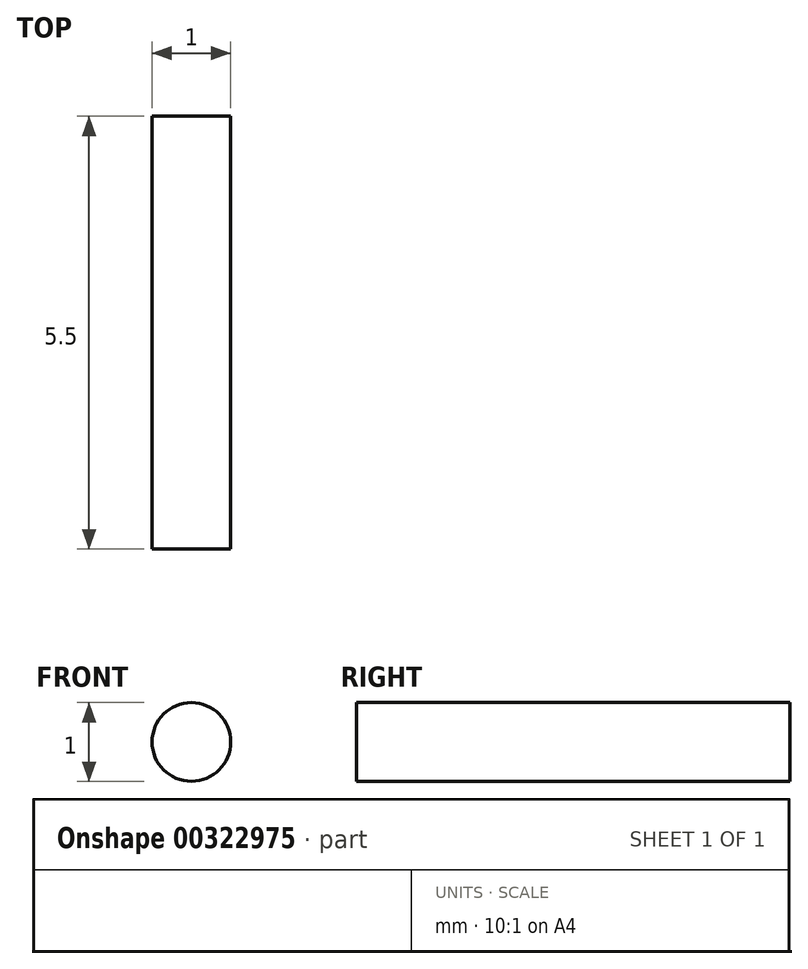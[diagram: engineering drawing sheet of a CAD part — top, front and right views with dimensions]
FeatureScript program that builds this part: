
annotation { "Feature Type Name" : "Feature", "Feature Type Description" : "" }
export const myFeature = defineFeature(function(context is Context, id is Id, definition is map)
    precondition{}
    {
        {
            var Q0;
            Q0=qCreatedBy(makeId("Front.planeOp"),FACE);
            var sketch = newSketch(context, id + "F0", { "sketchPlane" : qUnion([Q0])});
            skCircle(sketch, "E0", {"center": v(0, 0) * mm, "radius": 0.5 * mm});
            skSolve(sketch);
        }
        {
            var Q0;
            Q0=makeQuery(id+"F0.imprint","IMPRINT",FACE,{"disambiguationData":[TD([[makeQuery(id+"F0.imprint","IMPRINT",EDGE,{"derivedFrom":sQuery(id+"F0.wireOp",EDGE,"E0")}),1.0]])]});
            extrude(context, id + "F1", {"entities" : qUnion([Q0]), "depth" : 5.5 * mm, "symmetric" : true});
        }
    });
